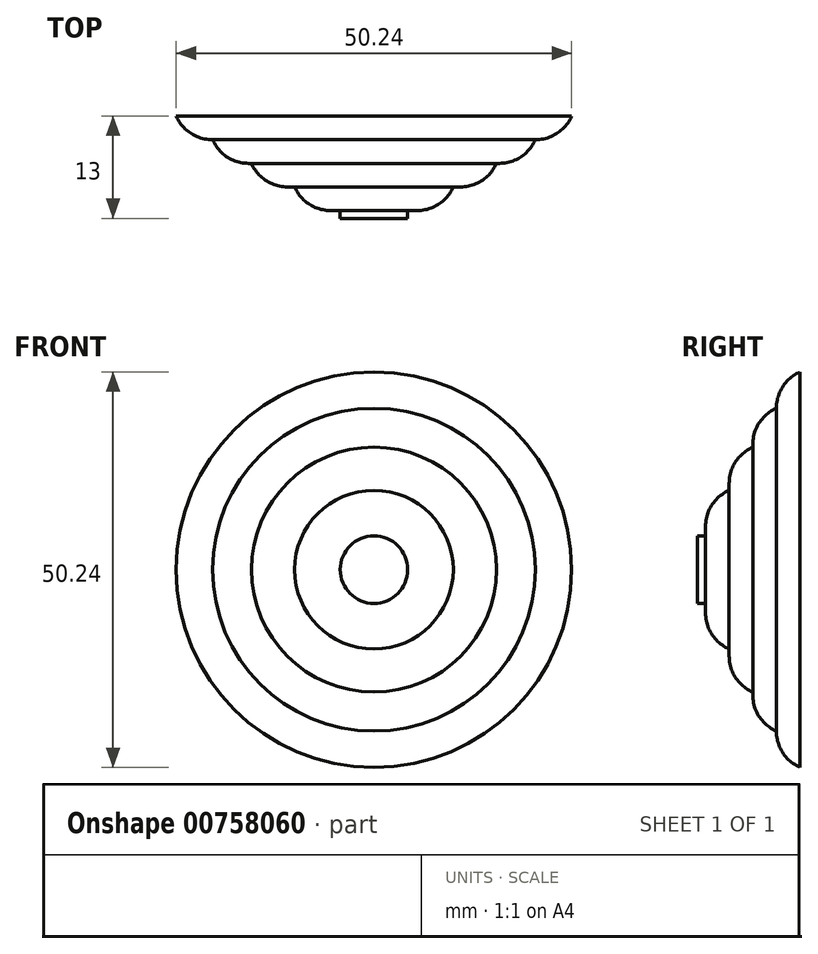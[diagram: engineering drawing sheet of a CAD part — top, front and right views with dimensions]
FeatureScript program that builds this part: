
annotation { "Feature Type Name" : "Feature", "Feature Type Description" : "" }
export const myFeature = defineFeature(function(context is Context, id is Id, definition is map)
    precondition{}
    {
        {
            var Q0;
            Q0=qCreatedBy(makeId("Front.planeOp"),FACE);
            var sketch = newSketch(context, id + "F0", { "sketchPlane" : qUnion([Q0])});
            skCircle(sketch, "E0", {"center": v(0, 0) * mm, "radius": 25.12 * mm});
            skCircle(sketch, "E1", {"center": v(0, 0) * mm, "radius": 20.5 * mm});
            skCircle(sketch, "E2", {"center": v(0, 0) * mm, "radius": 15.56 * mm});
            skCircle(sketch, "E3", {"center": v(0, 0) * mm, "radius": 10.08 * mm});
            skCircle(sketch, "E4", {"center": v(0, 0) * mm, "radius": 4.28 * mm});
            skCircle(sketch, "E5", {"center": v(0, 0) * mm, "radius": 1.25 * mm});
            skPoint(sketch, "E6", {"position": v(-3.12, 23.12) * mm});
            skPoint(sketch, "E7", {"position": v(2.92, 23.12) * mm});
            skPoint(sketch, "E8", {"position": v(-3.12, -22.8) * mm});
            skPoint(sketch, "E9", {"position": v(2.92, -22.4) * mm});
            skSolve(sketch);
        }
        {
            var Q0;
            Q0=makeQuery(id+"F0.imprint","IMPRINT",FACE,{"disambiguationData":[TD([[makeQuery(id+"F0.imprint","IMPRINT",EDGE,{"derivedFrom":sQuery(id+"F0.wireOp",EDGE,"E0")}),1.0]])]});
            extrude(context, id + "F1", {"entities" : qUnion([Q0]), "depth" : 3 * mm, "offsetDistance" : 25 * mm});
        }
        {
            var Q0;
            Q0=makeQuery(id+"F0.imprint","IMPRINT",FACE,{"disambiguationData":[TD([[makeQuery(id+"F0.imprint","IMPRINT",EDGE,{"derivedFrom":sQuery(id+"F0.wireOp",EDGE,"E1")}),1.0]])]});
            extrude(context, id + "F2", {"entities" : qUnion([Q0]), "operationType" : NewBodyOperationType.ADD, "depth" : 6 * mm, "offsetDistance" : 25 * mm});
        }
        {
            var Q0;
            Q0=makeQuery(id+"F0.imprint","IMPRINT",FACE,{"disambiguationData":[TD([[makeQuery(id+"F0.imprint","IMPRINT",EDGE,{"derivedFrom":sQuery(id+"F0.wireOp",EDGE,"E2")}),1.0]])]});
            extrude(context, id + "F3", {"entities" : qUnion([Q0]), "operationType" : NewBodyOperationType.ADD, "depth" : 9 * mm, "offsetDistance" : 25 * mm});
        }
        {
            var Q0;
            Q0=makeQuery(id+"F0.imprint","IMPRINT",FACE,{"disambiguationData":[TD([[makeQuery(id+"F0.imprint","IMPRINT",EDGE,{"derivedFrom":sQuery(id+"F0.wireOp",EDGE,"E3")}),1.0]])]});
            extrude(context, id + "F4", {"entities" : qUnion([Q0]), "operationType" : NewBodyOperationType.ADD, "depth" : 12 * mm, "offsetDistance" : 25 * mm});
        }
        {
            var Q0;
            Q0=makeQuery(id+"F0.imprint","IMPRINT",FACE,{"disambiguationData":[TD([[makeQuery(id+"F0.imprint","IMPRINT",EDGE,{"derivedFrom":sQuery(id+"F0.wireOp",EDGE,"E4")}),1.0]])]});
            extrude(context, id + "F5", {"entities" : qUnion([Q0]), "operationType" : NewBodyOperationType.ADD, "depth" : 13 * mm, "offsetDistance" : 25 * mm});
        }
        {
            var Q0;
            Q0=makeQuery(id+"F0.imprint","IMPRINT",FACE,{"disambiguationData":[TD([[makeQuery(id+"F0.imprint","IMPRINT",EDGE,{"derivedFrom":sQuery(id+"F0.wireOp",EDGE,"E5")}),1.0]])]});
            extrude(context, id + "F6", {"entities" : qUnion([Q0]), "operationType" : NewBodyOperationType.ADD, "depth" : 13 * mm, "offsetDistance" : 25 * mm});
        }
        {
            var Q0;
            Q0=makeQuery(id+"F1.opExtrude","CAP_EDGE",EDGE,{"disambiguationData":[OSD([sQuery(id+"F0.wireOp",EDGE,"E0")])],"isStart":false});
            var Q1;
            Q1=makeQuery(id+"F2.opExtrude","CAP_EDGE",EDGE,{"disambiguationData":[OSD([sQuery(id+"F0.wireOp",EDGE,"E1")])],"isStart":false});
            var Q2;
            Q2=makeQuery(id+"F3.opExtrude","CAP_EDGE",EDGE,{"disambiguationData":[OSD([sQuery(id+"F0.wireOp",EDGE,"E2")])],"isStart":false});
            var Q3;
            Q3=makeQuery(id+"F4.opExtrude","CAP_EDGE",EDGE,{"disambiguationData":[OSD([sQuery(id+"F0.wireOp",EDGE,"E3")])],"isStart":false});
            fillet(context, id + "F7", {"entities" : qUnion([Q0, Q1, Q2, Q3]), "radius" : 5 * mm, "tangentPropagation" : true, "allowEdgeOverflow" : false});
        }
    });
